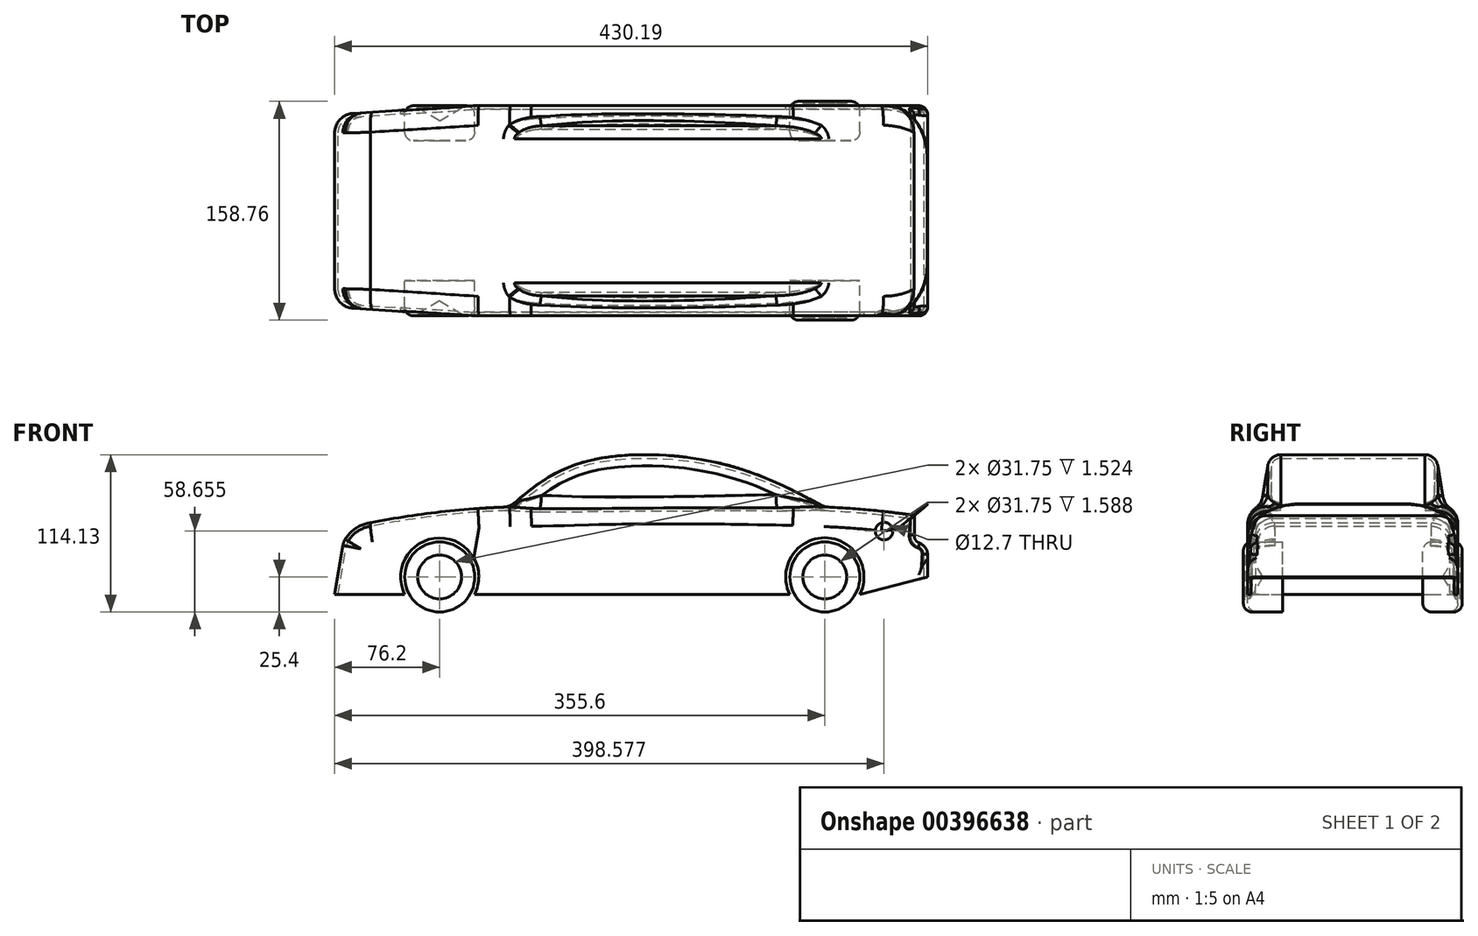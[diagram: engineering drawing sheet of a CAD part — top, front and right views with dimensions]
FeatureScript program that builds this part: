
annotation { "Feature Type Name" : "Feature", "Feature Type Description" : "" }
export const myFeature = defineFeature(function(context is Context, id is Id, definition is map)
    precondition{}
    {
        {
            var Q0;
            Q0=qCreatedBy(makeId("Front.planeOp"),FACE);
            var sketch = newSketch(context, id + "F0", { "sketchPlane" : qUnion([Q0])});
            skCircle(sketch, "E0", {"center": v(-152.4, 12.7) * mm, "radius": 25.4 * mm});
            skCircle(sketch, "E1", {"center": v(127, 12.7) * mm, "radius": 25.4 * mm});
            skLineSegment(sketch, "E2", {"start": v(152.4, 0) * mm, "end": v(201.59, 12.7) * mm});
            skLineSegment(sketch, "E3", {"start": v(201.59, 12.7) * mm, "end": v(201.59, 38.1) * mm});
            skLineSegment(sketch, "E4", {"start": v(201.59, 38.1) * mm, "end": v(191.93, 38.1) * mm});
            skLineSegment(sketch, "E5", {"start": v(191.93, 38.1) * mm, "end": v(191.93, 57.15) * mm});
            skLineSegment(sketch, "E6", {"start": v(191.93, 57.15) * mm, "end": v(201.59, 65.4) * mm});
            skLineSegment(sketch, "E7", {"start": v(201.59, 65.4) * mm, "end": v(201.26, 65.8) * mm});
            skLineSegment(sketch, "E8", {"start": v(201.26, 65.8) * mm, "end": v(191.6, 57.54) * mm});
            skPoint(sketch, "E9", {"position": v(-101.6, 63.5) * mm});
            skFitSpline(sketch, "E10", {"points": [v(127, 63.5) * mm, v(50.8, 95.24) * mm, v(-50.8, 95.24) * mm, v(-101.6, 63.5) * mm], "startDerivative": vector(-207.13, 110.1) * mm, "endDerivative": vector(-151.58, -130.46) * mm});
            skArc(sketch, "E11", {"start": v(-101.6, 63.5) * mm, "mid": v(-152.3, 59.8) * mm, "end": v(-202.55, 52.05) * mm});
            skLineSegment(sketch, "E12", {"start": v(-177.8, 0) * mm, "end": v(-228.6, 0) * mm});
            skLineSegment(sketch, "E13", {"start": v(-228.6, 0) * mm, "end": v(-222.25, 37.57) * mm});
            skArc(sketch, "E14", {"start": v(-202.55, 52.05) * mm, "mid": v(-214.26, 47.34) * mm, "end": v(-222.25, 37.57) * mm});
            skLineSegment(sketch, "E15", {"start": v(-127, 0) * mm, "end": v(101.6, 0) * mm});
            skLineSegment(sketch, "E16", {"start": v(152.4, 0) * mm, "end": v(152.4, 0) * mm});
            skArc(sketch, "E17.0", {"start": v(-127, 0) * mm, "mid": v(-152.4, 41.1) * mm, "end": v(-177.8, 0) * mm});
            skArc(sketch, "E18.0", {"start": v(152.4, 0) * mm, "mid": v(127, 41.1) * mm, "end": v(101.6, 0) * mm});
            skFitSpline(sketch, "E19", {"points": [v(-101.6, 63.5) * mm, v(127, 63.5) * mm, v(191.6, 57.54) * mm], "startDerivative": vector(404.05, 5.59) * mm, "endDerivative": vector(157.28, -20.11) * mm});
            skPoint(sketch, "E20", {"position": v(169.98, 45.96) * mm});
            skSolve(sketch);
        }
        {
            var Q0;
            {var subQ3=sQuery(id+"F0.wireOp",EDGE,"E2");Q0=makeQuery(id+"F0.imprint","IMPRINT",FACE,{"disambiguationData":[TD([[makeQuery(id+"F0.imprint","IMPRINT",EDGE,{"derivedFrom":subQ3}),1.0]])]});}
            extrude(context, id + "F1", {"entities" : qUnion([Q0]), "endBound" : BoundingType.SYMMETRIC, "depth" : 152.4 * mm});
        }
        {
            var Q0;
            Q0=makeQuery(id+"F0.imprint","IMPRINT",FACE,{"disambiguationData":[TD([[makeQuery(id+"F0.imprint","IMPRINT",EDGE,{"derivedFrom":sQuery(id+"F0.wireOp",EDGE,"E0")}),1.0]])]});
            extrude(context, id + "F2", {"entities" : qUnion([Q0]), "endBound" : BoundingType.SYMMETRIC, "depth" : 152.4 * mm});
        }
        {
            var Q0;
            {var subQ0=sQuery(id+"F0.wireOp",EDGE,"E1");var subQ1=makeQuery(id+"F0.imprint","INTERSECT",VERTEX,{"derivedFrom":[subQ0,sQuery(id+"F0.wireOp",EDGE,"E2")]});Q0=makeQuery(id+"F0.imprint","IMPRINT",FACE,{"disambiguationData":[TD([[makeQuery(id+"F0.imprint","IMPRINT",EDGE,{"disambiguationData":[TD([[subQ1,-1.0]])],"derivedFrom":subQ0}),1.0]])]});}
            extrude(context, id + "F3", {"entities" : qUnion([Q0]), "endBound" : BoundingType.SYMMETRIC, "depth" : 158.75 * mm});
        }
        {
            var Q0;
            {var subQ0=sQuery(id+"F0.wireOp",EDGE,"E0");var subQ1=makeQuery(id+"F0.imprint","INTERSECT",VERTEX,{"derivedFrom":[subQ0,sQuery(id+"F0.wireOp",EDGE,"E12")]});Q0=makeQuery(id+"F0.imprint","IMPRINT",FACE,{"disambiguationData":[TD([[makeQuery(id+"F0.imprint","IMPRINT",EDGE,{"disambiguationData":[TD([[subQ1,1.0]])],"derivedFrom":subQ0}),1.0]])]});}
            var Q1;
            {var subQ0=sQuery(id+"F0.wireOp",EDGE,"E1");var subQ1=makeQuery(id+"F0.imprint","INTERSECT",VERTEX,{"derivedFrom":[subQ0,sQuery(id+"F0.wireOp",EDGE,"E2")]});Q1=makeQuery(id+"F0.imprint","IMPRINT",FACE,{"disambiguationData":[TD([[makeQuery(id+"F0.imprint","IMPRINT",EDGE,{"disambiguationData":[TD([[subQ1,-1.0]])],"derivedFrom":subQ0}),1.0]])]});}
            extrude(context, id + "F4", {"entities" : qUnion([Q0, Q1]), "operationType" : NewBodyOperationType.REMOVE, "endBound" : BoundingType.SYMMETRIC, "oppositeDirection" : true, "depth" : 101.6 * mm});
        }
        {
            var Q0;
            {var subQ0=sQuery(id+"F0.wireOp",EDGE,"E10");Q0=makeQuery(id+"F0.imprint","IMPRINT",FACE,{"disambiguationData":[TD([[makeQuery(id+"F0.imprint","IMPRINT",EDGE,{"derivedFrom":subQ0}),1.0]])]});}
            extrude(context, id + "F5", {"entities" : qUnion([Q0]), "operationType" : NewBodyOperationType.ADD, "endBound" : BoundingType.SYMMETRIC, "depth" : 133.35 * mm});
        }
        {
            var Q0;
            Q0=makeQuery(id+"F3.opExtrude","CAP_EDGE",EDGE,{"disambiguationData":[OSD([sQuery(id+"F0.wireOp",EDGE,"E0")])],"isStart":false});
            var Q1;
            Q1=makeQuery(id+"F3.opExtrude","CAP_EDGE",EDGE,{"disambiguationData":[OSD([sQuery(id+"F0.wireOp",EDGE,"E1")])],"isStart":false});
            var Q2;
            Q2=makeQuery(id+"F3.opExtrude","CAP_EDGE",EDGE,{"disambiguationData":[OSD([sQuery(id+"F0.wireOp",EDGE,"E0")])],"isStart":true});
            var Q3;
            Q3=makeQuery(id+"F3.opExtrude","CAP_EDGE",EDGE,{"disambiguationData":[OSD([sQuery(id+"F0.wireOp",EDGE,"E1")])],"isStart":true});
            var Q4;
            Q4=makeQuery(id+"F4.boolean.opBoolean","COPY",EDGE,{"derivedFrom":makeQuery(id+"F4.opExtrude","CAP_EDGE",EDGE,{"disambiguationData":[OSD([sQuery(id+"F0.wireOp",EDGE,"E1")])],"isStart":true})});
            var Q5;
            Q5=makeQuery(id+"F4.boolean.opBoolean","COPY",EDGE,{"derivedFrom":makeQuery(id+"F4.opExtrude","CAP_EDGE",EDGE,{"disambiguationData":[OSD([sQuery(id+"F0.wireOp",EDGE,"E0")])],"isStart":true})});
            var Q6;
            Q6=makeQuery(id+"F4.boolean.opBoolean","COPY",EDGE,{"derivedFrom":makeQuery(id+"F4.opExtrude","CAP_EDGE",EDGE,{"disambiguationData":[OSD([sQuery(id+"F0.wireOp",EDGE,"E0")])],"isStart":false})});
            var Q7;
            Q7=makeQuery(id+"F4.boolean.opBoolean","COPY",EDGE,{"derivedFrom":makeQuery(id+"F4.opExtrude","CAP_EDGE",EDGE,{"disambiguationData":[OSD([sQuery(id+"F0.wireOp",EDGE,"E1")])],"isStart":false})});
            var Q8;
            Q8=makeQuery(id+"F2.opExtrude","CAP_EDGE",EDGE,{"disambiguationData":[OSD([sQuery(id+"F0.wireOp",EDGE,"E0")])],"isStart":false});
            var Q9;
            Q9=makeQuery(id+"F2.opExtrude","CAP_EDGE",EDGE,{"disambiguationData":[OSD([sQuery(id+"F0.wireOp",EDGE,"E0")])],"isStart":true});
            fillet(context, id + "F6", {"entities" : qUnion([Q0, Q1, Q2, Q3, Q4, Q5, Q6, Q7, Q8, Q9]), "radius" : 6.35 * mm, "tangentPropagation" : true, "allowEdgeOverflow" : false});
        }
        {
            var Q0;
            Q0=makeQuery(id+"F5.opExtrude","CAP_EDGE",EDGE,{"disambiguationData":[OSD([sQuery(id+"F0.wireOp",EDGE,"E10")])],"isStart":false});
            chamfer(context, id + "F7", {"entities" : qUnion([Q0]), "chamferType" : ChamferType.TWO_OFFSETS, "width1" : 38.1 * mm, "oppositeDirection" : false, "width2" : 6.35 * mm, "tangentPropagation" : true});
        }
        {
            var Q0;
            Q0=makeQuery(id+"F5.opExtrude","CAP_EDGE",EDGE,{"disambiguationData":[OSD([sQuery(id+"F0.wireOp",EDGE,"E10")])],"isStart":true});
            chamfer(context, id + "F8", {"entities" : qUnion([Q0]), "chamferType" : ChamferType.TWO_OFFSETS, "width1" : 38.1 * mm, "oppositeDirection" : true, "width2" : 6.35 * mm, "tangentPropagation" : true});
        }
        {
            var Q0;
            Q0=makeQuery(id+"F1.opExtrude","CAP_EDGE",EDGE,{"disambiguationData":[OSD([sQuery(id+"F0.wireOp",EDGE,"E13")])],"isStart":true});
            var Q1;
            Q1=makeQuery(id+"F1.opExtrude","CAP_EDGE",EDGE,{"disambiguationData":[OSD([sQuery(id+"F0.wireOp",EDGE,"E13")])],"isStart":false});
            chamfer(context, id + "F9", {"entities" : qUnion([Q0, Q1]), "chamferType" : ChamferType.TWO_OFFSETS, "width1" : 95.25 * mm, "oppositeDirection" : false, "width2" : 6.35 * mm, "tangentPropagation" : true});
        }
        {
            var Q0;
            Q0=makeQuery(id+"F1.opExtrude","CAP_EDGE",EDGE,{"disambiguationData":[OSD([sQuery(id+"F0.wireOp",EDGE,"E5")])],"isStart":false});
            var Q1;
            Q1=makeQuery(id+"F1.opExtrude","CAP_EDGE",EDGE,{"disambiguationData":[OSD([sQuery(id+"F0.wireOp",EDGE,"E3")])],"isStart":false});
            var Q2;
            Q2=makeQuery(id+"F1.opExtrude","CAP_EDGE",EDGE,{"disambiguationData":[OSD([sQuery(id+"F0.wireOp",EDGE,"E5")])],"isStart":true});
            var Q3;
            Q3=makeQuery(id+"F1.opExtrude","CAP_EDGE",EDGE,{"disambiguationData":[OSD([sQuery(id+"F0.wireOp",EDGE,"E3")])],"isStart":true});
            fillet(context, id + "F10", {"entities" : qUnion([Q0, Q1, Q2, Q3]), "radius" : 6.35 * mm, "tangentPropagation" : true, "allowEdgeOverflow" : false});
        }
        {
            var Q0;
            {var subQ0=sQuery(id+"F0.wireOp",EDGE,"E10");Q0=makeQuery(id+"F7.opChamfer","BLEND_EDGE",EDGE,{"blendedFrom":[makeQuery(id+"F5.opExtrude","CAP_EDGE",EDGE,{"disambiguationData":[OSD([subQ0])],"isStart":false}),makeQuery(id+"F5.opExtrude","SWEPT_FACE",FACE,{"disambiguationData":[OSD([subQ0])]})],"blendedInto":[makeQuery(id+"F5.opExtrude","SWEPT_FACE",FACE,{"disambiguationData":[OSD([subQ0])]})]});}
            var Q1;
            {var subQ0=sQuery(id+"F0.wireOp",EDGE,"E10");Q1=makeQuery(id+"F8.opChamfer","BLEND_EDGE",EDGE,{"blendedFrom":[makeQuery(id+"F8ikng03V6ZvgNQ_1.opExtrude","CAP_EDGE",EDGE,{"disambiguationData":[OSD([subQ0])],"isStart":false}),makeQuery(id+"F8ikng03V6ZvgNQ_1.opExtrude","SWEPT_FACE",FACE,{"disambiguationData":[OSD([subQ0])]})],"blendedInto":[makeQuery(id+"F8ikng03V6ZvgNQ_1.opExtrude","SWEPT_FACE",FACE,{"disambiguationData":[OSD([subQ0])]})]});}
            var Q2;
            {var subQ0=sQuery(id+"F0.wireOp",EDGE,"E10");Q2=makeQuery(id+"F8.opChamfer","BLEND_EDGE",EDGE,{"blendedFrom":[makeQuery(id+"F5.opExtrude","CAP_EDGE",EDGE,{"disambiguationData":[OSD([subQ0])],"isStart":true}),makeQuery(id+"F5.opExtrude","SWEPT_FACE",FACE,{"disambiguationData":[OSD([subQ0])]})],"blendedInto":[makeQuery(id+"F5.opExtrude","SWEPT_FACE",FACE,{"disambiguationData":[OSD([subQ0])]})]});}
            fillet(context, id + "F11", {"entities" : qUnion([Q0, Q1, Q2]), "radius" : 9.65 * mm, "tangentPropagation" : true, "allowEdgeOverflow" : false});
        }
        {
            var Q0;
            Q0=makeQuery(id+"F1.opExtrude","CAP_EDGE",EDGE,{"disambiguationData":[OSD([sQuery(id+"F0.wireOp",EDGE,"E7")])],"isStart":false});
            var Q1;
            Q1=makeQuery(id+"F1.opExtrude","CAP_EDGE",EDGE,{"disambiguationData":[OSD([sQuery(id+"F0.wireOp",EDGE,"E7")])],"isStart":true});
            fillet(context, id + "F12", {"entities" : qUnion([Q0, Q1]), "radius" : 38.1 * mm, "tangentPropagation" : true, "allowEdgeOverflow" : false});
        }
        {
            var Q0;
            Q0=makeQuery(id+"F1.opExtrude","CAP_EDGE",EDGE,{"disambiguationData":[OSD([sQuery(id+"F0.wireOp",EDGE,"E13")])],"isStart":false});
            var Q1;
            Q1=makeQuery(id+"F1.opExtrude","CAP_EDGE",EDGE,{"disambiguationData":[OSD([sQuery(id+"F0.wireOp",EDGE,"E14")])],"isStart":false});
            var Q2;
            Q2=makeQuery(id+"F1.opExtrude","CAP_EDGE",EDGE,{"disambiguationData":[OSD([sQuery(id+"F0.wireOp",EDGE,"E11")])],"isStart":false});
            var Q3;
            Q3=makeQuery(id+"F1.opExtrude","CAP_EDGE",EDGE,{"disambiguationData":[OSD([sQuery(id+"F0.wireOp",EDGE,"E19")])],"isStart":false});
            var Q4;
            Q4=makeQuery(id+"F1.opExtrude","CAP_EDGE",EDGE,{"disambiguationData":[OSD([sQuery(id+"F0.wireOp",EDGE,"E13")])],"isStart":true});
            var Q5;
            Q5=makeQuery(id+"F1.opExtrude","CAP_EDGE",EDGE,{"disambiguationData":[OSD([sQuery(id+"F0.wireOp",EDGE,"E14")])],"isStart":true});
            var Q6;
            Q6=makeQuery(id+"F1.opExtrude","CAP_EDGE",EDGE,{"disambiguationData":[OSD([sQuery(id+"F0.wireOp",EDGE,"E11")])],"isStart":true});
            var Q7;
            Q7=makeQuery(id+"F1.opExtrude","CAP_EDGE",EDGE,{"disambiguationData":[OSD([sQuery(id+"F0.wireOp",EDGE,"E19")])],"isStart":true});
            var Q8;
            Q8=makeQuery(id+"F9.opChamfer","BLEND_EDGE",EDGE,{"blendedFrom":[makeQuery(id+"F1.opExtrude","CAP_EDGE",EDGE,{"disambiguationData":[OSD([sQuery(id+"F0.wireOp",EDGE,"E13")])],"isStart":true}),makeQuery(id+"F1.opExtrude","SWEPT_FACE",FACE,{"disambiguationData":[OSD([sQuery(id+"F0.wireOp",EDGE,"E14")])]})],"blendedInto":[makeQuery(id+"F1.opExtrude","SWEPT_FACE",FACE,{"disambiguationData":[OSD([sQuery(id+"F0.wireOp",EDGE,"E14")])]})]});
            var Q9;
            {var subQ0=sQuery(id+"F0.wireOp",EDGE,"E13");Q9=makeQuery(id+"F9.opChamfer","BLEND_EDGE",EDGE,{"blendedFrom":[makeQuery(id+"F1.opExtrude","CAP_EDGE",EDGE,{"disambiguationData":[OSD([subQ0])],"isStart":true}),makeQuery(id+"F1.opExtrude","SWEPT_FACE",FACE,{"disambiguationData":[OSD([subQ0])]})],"blendedInto":[makeQuery(id+"F1.opExtrude","SWEPT_FACE",FACE,{"disambiguationData":[OSD([subQ0])]})]});}
            var Q10;
            {var subQ0=sQuery(id+"F0.wireOp",EDGE,"E13");Q10=makeQuery(id+"F9.opChamfer","BLEND_EDGE",EDGE,{"blendedFrom":[makeQuery(id+"F1.opExtrude","CAP_EDGE",EDGE,{"disambiguationData":[OSD([subQ0])],"isStart":false}),makeQuery(id+"F1.opExtrude","SWEPT_FACE",FACE,{"disambiguationData":[OSD([subQ0])]})],"blendedInto":[makeQuery(id+"F1.opExtrude","SWEPT_FACE",FACE,{"disambiguationData":[OSD([subQ0])]})]});}
            var Q11;
            Q11=makeQuery(id+"F9.opChamfer","BLEND_EDGE",EDGE,{"blendedFrom":[makeQuery(id+"F1.opExtrude","CAP_EDGE",EDGE,{"disambiguationData":[OSD([sQuery(id+"F0.wireOp",EDGE,"E13")])],"isStart":false}),makeQuery(id+"F1.opExtrude","SWEPT_FACE",FACE,{"disambiguationData":[OSD([sQuery(id+"F0.wireOp",EDGE,"E14")])]})],"blendedInto":[makeQuery(id+"F1.opExtrude","SWEPT_FACE",FACE,{"disambiguationData":[OSD([sQuery(id+"F0.wireOp",EDGE,"E14")])]})]});
            fillet(context, id + "F13", {"entities" : qUnion([Q0, Q1, Q2, Q3, Q4, Q5, Q6, Q7, Q8, Q9, Q10, Q11]), "radius" : 14.22 * mm, "tangentPropagation" : true, "allowEdgeOverflow" : false});
        }
        {
            var Q0;
            Q0=makeQuery(id+"F12.opFillet","BLEND_EDGE",EDGE,{"blendedFrom":[makeQuery(id+"F1.opExtrude","CAP_EDGE",EDGE,{"disambiguationData":[OSD([sQuery(id+"F0.wireOp",EDGE,"E7")])],"isStart":false}),makeQuery(id+"F1.opExtrude","SWEPT_FACE",FACE,{"disambiguationData":[OSD([sQuery(id+"F0.wireOp",EDGE,"E3")])]})],"blendedInto":[makeQuery(id+"F1.opExtrude","SWEPT_FACE",FACE,{"disambiguationData":[OSD([sQuery(id+"F0.wireOp",EDGE,"E3")])]})]});
            var Q1;
            Q1=makeQuery(id+"F12.opFillet","BLEND_EDGE",EDGE,{"blendedFrom":[makeQuery(id+"FRxWjm23BxfcHbo_1.opExtrude","CAP_EDGE",EDGE,{"disambiguationData":[OSD([sQuery(id+"F0.wireOp",EDGE,"E7")])],"isStart":false}),makeQuery(id+"FRxWjm23BxfcHbo_1.opExtrude","SWEPT_FACE",FACE,{"disambiguationData":[OSD([sQuery(id+"F0.wireOp",EDGE,"E3")])]})],"blendedInto":[makeQuery(id+"FRxWjm23BxfcHbo_1.opExtrude","SWEPT_FACE",FACE,{"disambiguationData":[OSD([sQuery(id+"F0.wireOp",EDGE,"E3")])]})]});
            var Q2;
            Q2=makeQuery(id+"F1.opExtrude","SWEPT_EDGE",EDGE,{"disambiguationData":[OSD([sQuery(id+"F0.wireOp",EDGE,"E3"),sQuery(id+"F0.wireOp",EDGE,"E4")])]});
            var Q3;
            Q3=makeQuery(id+"FRxWjm23BxfcHbo_1.opExtrude","SWEPT_EDGE",EDGE,{"disambiguationData":[OSD([sQuery(id+"F0.wireOp",EDGE,"E3"),sQuery(id+"F0.wireOp",EDGE,"E4")])]});
            fillet(context, id + "F14", {"entities" : qUnion([Q0, Q1, Q2, Q3]), "radius" : 9.65 * mm, "tangentPropagation" : true, "allowEdgeOverflow" : false});
        }
        {
            var Q0;
            Q0=makeQuery(id+"F2.opExtrude","CAP_FACE",FACE,{"disambiguationData":[OSD([sQuery(id+"F0.wireOp",EDGE,"E0")])],"isStart":false});
            var Q1;
            Q1=makeQuery(id+"F3.opExtrude","CAP_FACE",FACE,{"disambiguationData":[OSD([sQuery(id+"F0.wireOp",EDGE,"E1")])],"isStart":false});
            cPlane(context, id + "F15", {"entities" : qUnion([Q0, Q1]), "cplaneType" : CPlaneType.MID_PLANE, "offset" : 25.4 * mm, "width" : 152.4 * mm, "height" : 152.4 * mm});
        }
        {
            var Q0;
            Q0=qCreatedBy(id+"F15.planeOp",FACE);
            var sketch = newSketch(context, id + "F16", { "sketchPlane" : qUnion([Q0])});
            skPoint(sketch, "E21", {"position": v(-152.4, 12.7) * mm});
            skPoint(sketch, "E22", {"position": v(127, 12.7) * mm});
            skSolve(sketch);
        }
        {
            var Q0;
            Q0=makeQuery(id+"F3.opExtrude","CAP_FACE",FACE,{"disambiguationData":[OSD([sQuery(id+"F0.wireOp",EDGE,"E1")])],"isStart":true});
            var Q1;
            Q1=makeQuery(id+"F2.opExtrude","CAP_FACE",FACE,{"disambiguationData":[OSD([sQuery(id+"F0.wireOp",EDGE,"E0")])],"isStart":true});
            cPlane(context, id + "F17", {"entities" : qUnion([Q0, Q1]), "cplaneType" : CPlaneType.MID_PLANE, "offset" : 25.4 * mm, "width" : 152.4 * mm, "height" : 152.4 * mm});
        }
        {
            var Q0;
            Q0=qCreatedBy(id+"F17.planeOp",FACE);
            var sketch = newSketch(context, id + "F18", { "sketchPlane" : qUnion([Q0])});
            skPoint(sketch, "E23", {"position": v(-127, 12.7) * mm});
            skPoint(sketch, "E24", {"position": v(152.4, 12.7) * mm});
            skSolve(sketch);
        }
        {
            var Q0;
            Q0=sQuery(id+"F16.wireOp",VERTEX,"E21");
            var Q1;
            Q1=sQuery(id+"F18.wireOp",VERTEX,"E24");
            var Q2;
            Q2=makeQuery(id+"F4.boolean.opBoolean","SPLIT",BODY,{"disambiguationData":[OD(0.0)],"derivedFrom":makeQuery(id+"F3.opExtrude","SWEPT_BODY",BODY,{"disambiguationData":[OSD([sQuery(id+"F0.wireOp",EDGE,"E0")])]})});
            var Q3;
            Q3=makeQuery(id+"F4.boolean.opBoolean","SPLIT",BODY,{"disambiguationData":[OD(0.0)],"derivedFrom":makeQuery(id+"F3.opExtrude","SWEPT_BODY",BODY,{"disambiguationData":[OSD([sQuery(id+"F0.wireOp",EDGE,"E1")])]})});
            var Q4;
            Q4=makeQuery(id+"F4.boolean.opBoolean","SPLIT",BODY,{"disambiguationData":[OD(1.0)],"derivedFrom":makeQuery(id+"F3.opExtrude","SWEPT_BODY",BODY,{"disambiguationData":[OSD([sQuery(id+"F0.wireOp",EDGE,"E1")])]})});
            var Q5;
            Q5=makeQuery(id+"F4.boolean.opBoolean","SPLIT",BODY,{"disambiguationData":[OD(1.0)],"derivedFrom":makeQuery(id+"F3.opExtrude","SWEPT_BODY",BODY,{"disambiguationData":[OSD([sQuery(id+"F0.wireOp",EDGE,"E0")])]})});
            var Q6;
            Q6=makeQuery(id+"F4.boolean.opBoolean","SPLIT",BODY,{"disambiguationData":[OD(1.0)],"derivedFrom":makeQuery(id+"F2.opExtrude","SWEPT_BODY",BODY,{"disambiguationData":[OSD([sQuery(id+"F0.wireOp",EDGE,"E0")])]})});
            var Q7;
            Q7=makeQuery(id+"F4.boolean.opBoolean","SPLIT",BODY,{"disambiguationData":[OD(0.0)],"derivedFrom":makeQuery(id+"F2.opExtrude","SWEPT_BODY",BODY,{"disambiguationData":[OSD([sQuery(id+"F0.wireOp",EDGE,"E0")])]})});
            hole(context, id + "F19", {"style" : HoleStyle.SIMPLE, "endStyle" : HoleEndStyle.BLIND, "holeDiameter" : 31.75 * mm, "holeDepth" : 1.52 * mm, "isTappedThrough" : true, "tappedDepth" : 12.7 * mm, "tapClearance" : 3, "locations" : qUnion([Q0, Q1]), "scope" : qUnion([Q2, Q3, Q4, Q5, Q6, Q7])});
        }
        {
            var Q0;
            Q0=sQuery(id+"F16.wireOp",VERTEX,"E22");
            var Q1;
            Q1=sQuery(id+"F18.wireOp",VERTEX,"E23");
            var Q2;
            Q2=makeQuery(id+"F4.boolean.opBoolean","SPLIT",BODY,{"disambiguationData":[OD(0.0)],"derivedFrom":makeQuery(id+"F3.opExtrude","SWEPT_BODY",BODY,{"disambiguationData":[OSD([sQuery(id+"F0.wireOp",EDGE,"E1")])]})});
            var Q3;
            Q3=makeQuery(id+"F4.boolean.opBoolean","SPLIT",BODY,{"disambiguationData":[OD(1.0)],"derivedFrom":makeQuery(id+"F3.opExtrude","SWEPT_BODY",BODY,{"disambiguationData":[OSD([sQuery(id+"F0.wireOp",EDGE,"E1")])]})});
            hole(context, id + "F20", {"style" : HoleStyle.SIMPLE, "endStyle" : HoleEndStyle.BLIND, "oppositeDirection" : true, "holeDiameter" : 31.75 * mm, "holeDepth" : 4.76 * mm, "isTappedThrough" : true, "tappedDepth" : 12.7 * mm, "tapClearance" : 3, "locations" : qUnion([Q0, Q1]), "scope" : qUnion([Q2, Q3])});
        }
        {
            var Q0;
            Q0=makeQuery(id+"F10.opFillet","BLEND_EDGE",EDGE,{"blendedFrom":[makeQuery(id+"F1.opExtrude","CAP_EDGE",EDGE,{"disambiguationData":[OSD([sQuery(id+"F0.wireOp",EDGE,"E5")])],"isStart":true}),makeQuery(id+"F1.opExtrude","SWEPT_FACE",FACE,{"disambiguationData":[OSD([sQuery(id+"F0.wireOp",EDGE,"E4")])]})],"blendedInto":[makeQuery(id+"F1.opExtrude","SWEPT_FACE",FACE,{"disambiguationData":[OSD([sQuery(id+"F0.wireOp",EDGE,"E4")])]})]});
            var Q1;
            Q1=makeQuery(id+"F10.opFillet","BLEND_EDGE",EDGE,{"blendedFrom":[makeQuery(id+"F1.opExtrude","CAP_EDGE",EDGE,{"disambiguationData":[OSD([sQuery(id+"F0.wireOp",EDGE,"E5")])],"isStart":false}),makeQuery(id+"F1.opExtrude","SWEPT_FACE",FACE,{"disambiguationData":[OSD([sQuery(id+"F0.wireOp",EDGE,"E4")])]})],"blendedInto":[makeQuery(id+"F1.opExtrude","SWEPT_FACE",FACE,{"disambiguationData":[OSD([sQuery(id+"F0.wireOp",EDGE,"E4")])]})]});
            fillet(context, id + "F21", {"entities" : qUnion([Q0, Q1]), "radius" : 5.08 * mm, "tangentPropagation" : true, "allowEdgeOverflow" : false});
        }
        {
            var Q0;
            {var subQ0=sQuery(id+"F0.wireOp",EDGE,"E7");Q0=makeQuery(id+"F14.opFillet","BLEND_EDGE",EDGE,{"blendedFrom":[makeQuery(id+"F1.opExtrude","SWEPT_EDGE",EDGE,{"disambiguationData":[OSD([sQuery(id+"F0.wireOp",EDGE,"E3"),sQuery(id+"F0.wireOp",EDGE,"E4")])]}),makeQuery(id+"F12.opFillet","BLEND_FACE",FACE,{"disambiguationData":[OSD([subQ0]),TDD([makeQuery(id+"F1.opExtrude","CAP_EDGE",EDGE,{"disambiguationData":[OSD([subQ0])],"isStart":false})])]})],"blendedInto":[makeQuery(id+"F12.opFillet","BLEND_FACE",FACE,{"disambiguationData":[OSD([subQ0]),TDD([makeQuery(id+"F1.opExtrude","CAP_EDGE",EDGE,{"disambiguationData":[OSD([subQ0])],"isStart":false})])]})]});}
            var Q1;
            {var subQ0=sQuery(id+"F0.wireOp",EDGE,"E7");Q1=makeQuery(id+"F14.opFillet","BLEND_EDGE",EDGE,{"blendedFrom":[makeQuery(id+"F1.opExtrude","SWEPT_EDGE",EDGE,{"disambiguationData":[OSD([sQuery(id+"F0.wireOp",EDGE,"E3"),sQuery(id+"F0.wireOp",EDGE,"E4")])]}),makeQuery(id+"F12.opFillet","BLEND_FACE",FACE,{"disambiguationData":[OSD([subQ0]),TDD([makeQuery(id+"F1.opExtrude","CAP_EDGE",EDGE,{"disambiguationData":[OSD([subQ0])],"isStart":true})])]})],"blendedInto":[makeQuery(id+"F12.opFillet","BLEND_FACE",FACE,{"disambiguationData":[OSD([subQ0]),TDD([makeQuery(id+"F1.opExtrude","CAP_EDGE",EDGE,{"disambiguationData":[OSD([subQ0])],"isStart":true})])]})]});}
            fillet(context, id + "F22", {"entities" : qUnion([Q0, Q1]), "radius" : 5.08 * mm, "tangentPropagation" : true, "allowEdgeOverflow" : false});
        }
        {
            var Q0;
            Q0=makeQuery(id+"F13.opFillet","BLEND_EDGE",EDGE,{"blendedFrom":[makeQuery(id+"F1.opExtrude","CAP_EDGE",EDGE,{"disambiguationData":[OSD([sQuery(id+"F0.wireOp",EDGE,"E19")])],"isStart":false}),makeQuery(id+"F7.opChamfer","BLEND_FACE",FACE,{"disambiguationData":[OSD([sQuery(id+"F0.wireOp",EDGE,"E10")])]})],"blendedInto":[makeQuery(id+"F7.opChamfer","BLEND_FACE",FACE,{"disambiguationData":[OSD([sQuery(id+"F0.wireOp",EDGE,"E10")])]})]});
            var Q1;
            {var subQ0=sQuery(id+"F0.wireOp",EDGE,"E19");var subQ1=sQuery(id+"F0.wireOp",EDGE,"E11");var subQ2=sQuery(id+"F0.wireOp",EDGE,"E10");Q1=makeQuery(id+"F5.boolean.opBoolean","MERGE",EDGE,{"derivedFrom":[makeQuery(id+"F1.opExtrude","SWEPT_EDGE",EDGE,{"disambiguationData":[OSD([subQ2,subQ1,subQ0])]}),makeQuery(id+"F5.opExtrude","SWEPT_EDGE",EDGE,{"disambiguationData":[OSD([subQ2,subQ1,subQ0])]})]});}
            var Q2;
            Q2=makeQuery(id+"F13.opFillet","BLEND_EDGE",EDGE,{"blendedFrom":[makeQuery(id+"F1.opExtrude","CAP_EDGE",EDGE,{"disambiguationData":[OSD([sQuery(id+"F0.wireOp",EDGE,"E19")])],"isStart":true}),makeQuery(id+"F8.opChamfer","BLEND_FACE",FACE,{"disambiguationData":[OSD([sQuery(id+"F0.wireOp",EDGE,"E10")])]})],"blendedInto":[makeQuery(id+"F8.opChamfer","BLEND_FACE",FACE,{"disambiguationData":[OSD([sQuery(id+"F0.wireOp",EDGE,"E10")])]})]});
            var Q3;
            {var subQ0=sQuery(id+"F0.wireOp",EDGE,"E10");Q3=makeQuery(id+"F11.opFillet","BLEND_EDGE",EDGE,{"disambiguationData":[OD(0.0)],"blendedFrom":[makeQuery(id+"F8.opChamfer","BLEND_EDGE",EDGE,{"blendedFrom":[makeQuery(id+"F5.opExtrude","CAP_EDGE",EDGE,{"disambiguationData":[OSD([subQ0])],"isStart":true}),makeQuery(id+"F5.opExtrude","SWEPT_FACE",FACE,{"disambiguationData":[OSD([subQ0])]})],"blendedInto":[makeQuery(id+"F5.opExtrude","SWEPT_FACE",FACE,{"disambiguationData":[OSD([subQ0])]})]}),makeQuery(id+"F1.opExtrude","SWEPT_FACE",FACE,{"disambiguationData":[OSD([sQuery(id+"F0.wireOp",EDGE,"E19")])]})],"blendedInto":[makeQuery(id+"F1.opExtrude","SWEPT_FACE",FACE,{"disambiguationData":[OSD([sQuery(id+"F0.wireOp",EDGE,"E19")])]})]});}
            var Q4;
            Q4=makeQuery(id+"F8.opChamfer","BLEND_EDGE",EDGE,{"blendedFrom":[makeQuery(id+"F5.opExtrude","CAP_EDGE",EDGE,{"disambiguationData":[OSD([sQuery(id+"F0.wireOp",EDGE,"E10")])],"isStart":true}),makeQuery(id+"F1.opExtrude","SWEPT_FACE",FACE,{"disambiguationData":[OSD([sQuery(id+"F0.wireOp",EDGE,"E19")])]})],"blendedInto":[makeQuery(id+"F1.opExtrude","SWEPT_FACE",FACE,{"disambiguationData":[OSD([sQuery(id+"F0.wireOp",EDGE,"E19")])]})]});
            var Q5;
            Q5=makeQuery(id+"F5.opExtrude","SWEPT_EDGE",EDGE,{"disambiguationData":[OSD([sQuery(id+"F0.wireOp",EDGE,"E10"),sQuery(id+"F0.wireOp",EDGE,"E19")])]});
            var Q6;
            Q6=makeQuery(id+"F7.opChamfer","BLEND_EDGE",EDGE,{"blendedFrom":[makeQuery(id+"F5.opExtrude","CAP_EDGE",EDGE,{"disambiguationData":[OSD([sQuery(id+"F0.wireOp",EDGE,"E10")])],"isStart":false}),makeQuery(id+"F1.opExtrude","SWEPT_FACE",FACE,{"disambiguationData":[OSD([sQuery(id+"F0.wireOp",EDGE,"E19")])]})],"blendedInto":[makeQuery(id+"F1.opExtrude","SWEPT_FACE",FACE,{"disambiguationData":[OSD([sQuery(id+"F0.wireOp",EDGE,"E19")])]})]});
            var Q7;
            {var subQ0=sQuery(id+"F0.wireOp",EDGE,"E10");Q7=makeQuery(id+"F11.opFillet","BLEND_EDGE",EDGE,{"disambiguationData":[OD(0.0)],"blendedFrom":[makeQuery(id+"F7.opChamfer","BLEND_EDGE",EDGE,{"blendedFrom":[makeQuery(id+"F5.opExtrude","CAP_EDGE",EDGE,{"disambiguationData":[OSD([subQ0])],"isStart":false}),makeQuery(id+"F5.opExtrude","SWEPT_FACE",FACE,{"disambiguationData":[OSD([subQ0])]})],"blendedInto":[makeQuery(id+"F5.opExtrude","SWEPT_FACE",FACE,{"disambiguationData":[OSD([subQ0])]})]}),makeQuery(id+"F1.opExtrude","SWEPT_FACE",FACE,{"disambiguationData":[OSD([sQuery(id+"F0.wireOp",EDGE,"E19")])]})],"blendedInto":[makeQuery(id+"F1.opExtrude","SWEPT_FACE",FACE,{"disambiguationData":[OSD([sQuery(id+"F0.wireOp",EDGE,"E19")])]})]});}
            var Q8;
            {var subQ0=sQuery(id+"F0.wireOp",EDGE,"E10");Q8=makeQuery(id+"F11.opFillet","BLEND_EDGE",EDGE,{"disambiguationData":[OD(1.0)],"blendedFrom":[makeQuery(id+"F7.opChamfer","BLEND_EDGE",EDGE,{"blendedFrom":[makeQuery(id+"F5.opExtrude","CAP_EDGE",EDGE,{"disambiguationData":[OSD([subQ0])],"isStart":false}),makeQuery(id+"F5.opExtrude","SWEPT_FACE",FACE,{"disambiguationData":[OSD([subQ0])]})],"blendedInto":[makeQuery(id+"F5.opExtrude","SWEPT_FACE",FACE,{"disambiguationData":[OSD([subQ0])]})]}),makeQuery(id+"F1.opExtrude","SWEPT_FACE",FACE,{"disambiguationData":[OSD([sQuery(id+"F0.wireOp",EDGE,"E19")])]})],"blendedInto":[makeQuery(id+"F1.opExtrude","SWEPT_FACE",FACE,{"disambiguationData":[OSD([sQuery(id+"F0.wireOp",EDGE,"E19")])]})]});}
            var Q9;
            {var subQ0=sQuery(id+"F0.wireOp",EDGE,"E10");Q9=makeQuery(id+"F11.opFillet","BLEND_EDGE",EDGE,{"disambiguationData":[OD(1.0)],"blendedFrom":[makeQuery(id+"F8.opChamfer","BLEND_EDGE",EDGE,{"blendedFrom":[makeQuery(id+"F5.opExtrude","CAP_EDGE",EDGE,{"disambiguationData":[OSD([subQ0])],"isStart":true}),makeQuery(id+"F5.opExtrude","SWEPT_FACE",FACE,{"disambiguationData":[OSD([subQ0])]})],"blendedInto":[makeQuery(id+"F5.opExtrude","SWEPT_FACE",FACE,{"disambiguationData":[OSD([subQ0])]})]}),makeQuery(id+"F1.opExtrude","SWEPT_FACE",FACE,{"disambiguationData":[OSD([sQuery(id+"F0.wireOp",EDGE,"E19")])]})],"blendedInto":[makeQuery(id+"F1.opExtrude","SWEPT_FACE",FACE,{"disambiguationData":[OSD([sQuery(id+"F0.wireOp",EDGE,"E19")])]})]});}
            fillet(context, id + "F23", {"entities" : qUnion([Q0, Q1, Q2, Q3, Q4, Q5, Q6, Q7, Q8, Q9]), "radius" : 12.7 * mm, "tangentPropagation" : true, "allowEdgeOverflow" : false});
        }
        {
            var Q0;
            Q0=makeQuery(id+"F1.opExtrude","SWEPT_EDGE",EDGE,{"disambiguationData":[OSD([sQuery(id+"F0.wireOp",EDGE,"E13"),sQuery(id+"F0.wireOp",EDGE,"E14")])]});
            var Q1;
            Q1=makeQuery(id+"F13.opFillet","BLEND_EDGE",EDGE,{"blendedFrom":[makeQuery(id+"F1.opExtrude","CAP_EDGE",EDGE,{"disambiguationData":[OSD([sQuery(id+"F0.wireOp",EDGE,"E13")])],"isStart":false}),makeQuery(id+"F1.opExtrude","CAP_EDGE",EDGE,{"disambiguationData":[OSD([sQuery(id+"F0.wireOp",EDGE,"E14")])],"isStart":false})],"blendedInto":[]});
            fillet(context, id + "F24", {"entities" : qUnion([Q0, Q1]), "radius" : 12.7 * mm, "tangentPropagation" : true, "allowEdgeOverflow" : false});
        }
        {
            var Q0;
            Q0=makeQuery(id+"F1.opExtrude","SWEPT_FACE",FACE,{"disambiguationData":[OSD([sQuery(id+"F0.wireOp",EDGE,"E12")])]});
            var Q1;
            Q1=makeQuery(id+"F1.opExtrude","SWEPT_FACE",FACE,{"disambiguationData":[OSD([sQuery(id+"F0.wireOp",EDGE,"E17.0")])]});
            var Q2;
            Q2=makeQuery(id+"F1.opExtrude","SWEPT_FACE",FACE,{"disambiguationData":[OSD([sQuery(id+"F0.wireOp",EDGE,"E15")])]});
            var Q3;
            Q3=makeQuery(id+"F1.opExtrude","SWEPT_FACE",FACE,{"disambiguationData":[OSD([sQuery(id+"F0.wireOp",EDGE,"E18.0")])]});
            var Q4;
            Q4=makeQuery(id+"F1.opExtrude","SWEPT_FACE",FACE,{"disambiguationData":[OSD([sQuery(id+"F0.wireOp",EDGE,"E2"),sQuery(id+"F0.wireOp",EDGE,"E16")])]});
            shell(context, id + "F25", {"entities" : qUnion([Q0, Q1, Q2, Q3, Q4]), "thickness" : 2.54 * mm});
        }
        {
            var Q0;
            Q0=sQuery(id+"F0.wireOp",VERTEX,"E20");
            var Q1;
            Q1=makeQuery(id+"F1.opExtrude","SWEPT_BODY",BODY,{"disambiguationData":[OSD([sQuery(id+"F0.wireOp",EDGE,"E2"),sQuery(id+"F0.wireOp",EDGE,"E3"),sQuery(id+"F0.wireOp",EDGE,"E4"),sQuery(id+"F0.wireOp",EDGE,"E5"),sQuery(id+"F0.wireOp",EDGE,"E6"),sQuery(id+"F0.wireOp",EDGE,"E7"),sQuery(id+"F0.wireOp",EDGE,"E8"),sQuery(id+"F0.wireOp",EDGE,"E11"),sQuery(id+"F0.wireOp",EDGE,"E12"),sQuery(id+"F0.wireOp",EDGE,"E13"),sQuery(id+"F0.wireOp",EDGE,"E14"),sQuery(id+"F0.wireOp",EDGE,"E15"),sQuery(id+"F0.wireOp",EDGE,"E16"),sQuery(id+"F0.wireOp",EDGE,"E17.0"),sQuery(id+"F0.wireOp",EDGE,"E18.0"),sQuery(id+"F0.wireOp",EDGE,"E19")])]});
            hole(context, id + "F26", {"style" : HoleStyle.SIMPLE, "endStyle" : HoleEndStyle.THROUGH, "oppositeDirection" : true, "holeDiameter" : 12.7 * mm, "isTappedThrough" : true, "tappedDepth" : 12.7 * mm, "tapClearance" : 3, "locations" : qUnion([Q0]), "scope" : qUnion([Q1])});
        }
    });
